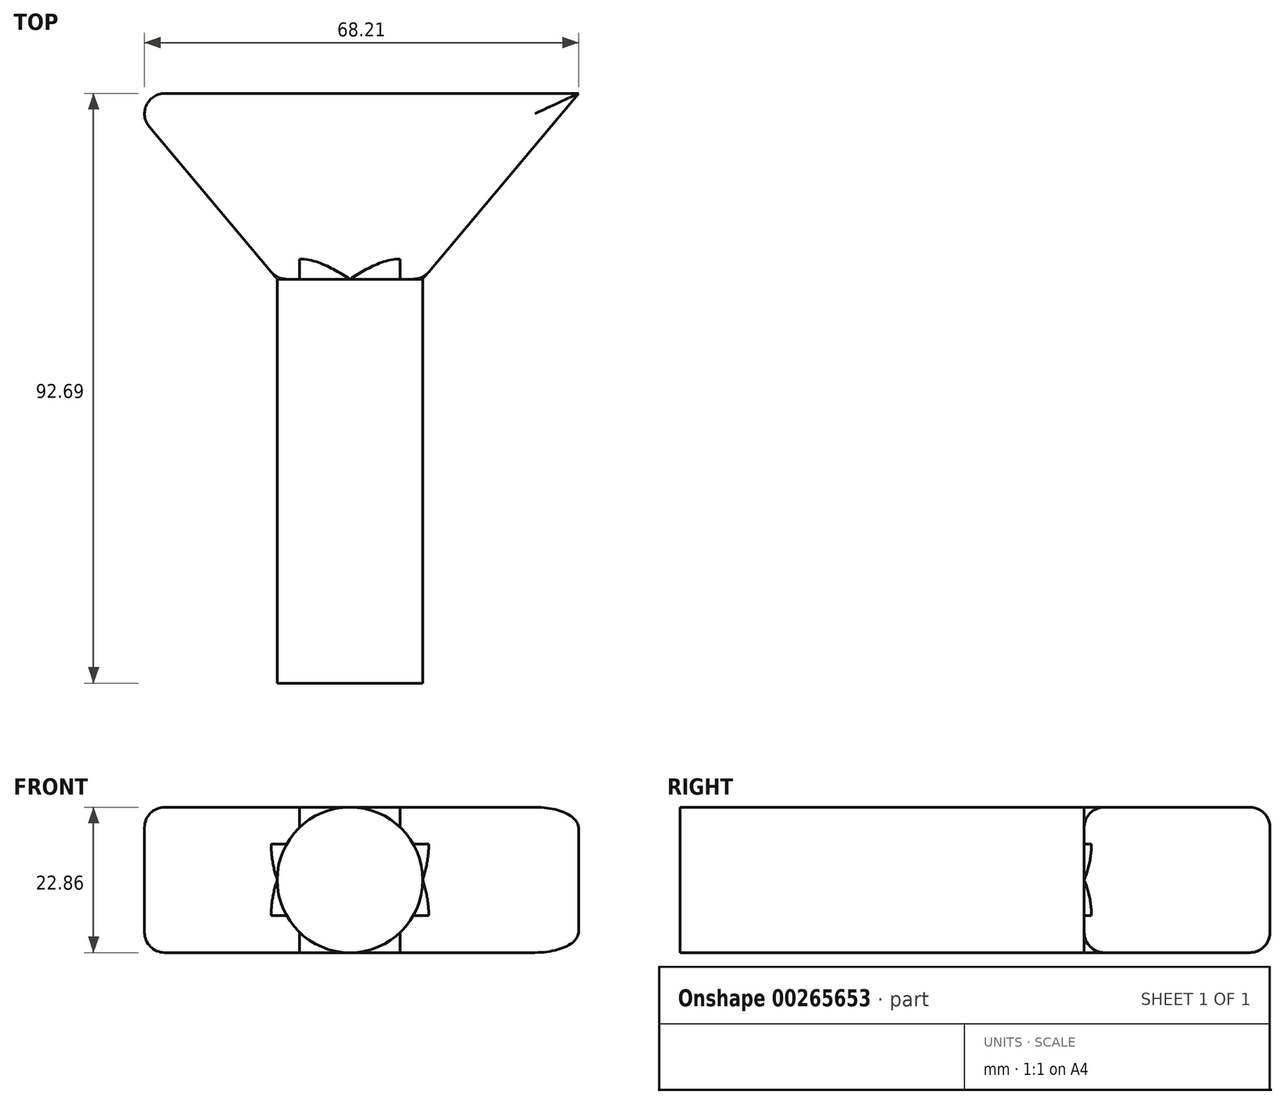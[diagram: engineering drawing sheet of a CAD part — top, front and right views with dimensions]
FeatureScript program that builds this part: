
annotation { "Feature Type Name" : "Feature", "Feature Type Description" : "" }
export const myFeature = defineFeature(function(context is Context, id is Id, definition is map)
    precondition{}
    {
        {
            var Q0;
            Q0=qCreatedBy(makeId("Top.planeOp"),FACE);
            var sketch = newSketch(context, id + "F0", { "sketchPlane" : qUnion([Q0])});
            skLineSegment(sketch, "E0", {"start": v(11.43, 0) * mm, "end": v(35.92, 29.19) * mm});
            skLineSegment(sketch, "E1", {"start": v(-11.43, 0) * mm, "end": v(-35.92, 29.19) * mm});
            skLineSegment(sketch, "E2", {"start": v(-35.92, 29.19) * mm, "end": v(35.92, 29.19) * mm});
            skLineSegment(sketch, "E3", {"start": v(-11.43, 0) * mm, "end": v(11.43, 0) * mm});
            skSolve(sketch);
        }
        {
            var Q0;
            Q0 = qSketchRegion(id + "F0", true);
            extrude(context, id + "F1", {"entities" : qUnion([Q0]), "depth" : 22.86 * mm});
        }
        {
            var Q0;
            Q0=makeQuery(id+"F1.opExtrude","SWEPT_FACE",FACE,{"disambiguationData":[OSD([sQuery(id+"F0.wireOp",EDGE,"E3")])]});
            var sketch = newSketch(context, id + "F2", { "sketchPlane" : qUnion([Q0])});
            skCircle(sketch, "E4", {"center": v(0, 11.43) * mm, "radius": 11.43 * mm});
            skPoint(sketch, "E4.centerSnap0", {"position": v(-11.43, 11.43) * mm});
            skSolve(sketch);
        }
        {
            var Q0;
            {var subQ0=sQuery(id+"F2.wireOp",EDGE,"E4");var subQ1=sQuery(id+"F0.wireOp",EDGE,"E3");var subQ2=makeQuery(id+"F2.imprint","INTERSECT",VERTEX,{"derivedFrom":[makeQuery(id+"F1.opExtrude","CAP_EDGE",EDGE,{"disambiguationData":[OSD([subQ1])],"isStart":false}),subQ0]});Q0=makeQuery(id+"F2.imprint","IMPRINT",FACE,{"disambiguationData":[TD([[makeQuery(id+"F2.imprint","IMPRINT",EDGE,{"disambiguationData":[TD([[subQ2,1.0]])],"derivedFrom":subQ0}),1.0]])]});}
            extrude(context, id + "F3", {"entities" : qUnion([Q0]), "operationType" : NewBodyOperationType.ADD, "depth" : 63.5 * mm});
        }
        {
            var Q0;
            Q0=makeQuery(id+"F1.opExtrude","CAP_EDGE",EDGE,{"disambiguationData":[OSD([sQuery(id+"F0.wireOp",EDGE,"E0")])],"isStart":false});
            var Q1;
            Q1=makeQuery(id+"F1.opExtrude","CAP_EDGE",EDGE,{"disambiguationData":[OSD([sQuery(id+"F0.wireOp",EDGE,"E1")])],"isStart":false});
            var Q2;
            Q2=makeQuery(id+"F1.opExtrude","CAP_FACE",FACE,{"disambiguationData":[OSD([sQuery(id+"F0.wireOp",EDGE,"E0"),sQuery(id+"F0.wireOp",EDGE,"E1"),sQuery(id+"F0.wireOp",EDGE,"E2"),sQuery(id+"F0.wireOp",EDGE,"E3")])],"isStart":false});
            var Q3;
            Q3=makeQuery(id+"F1.opExtrude","CAP_EDGE",EDGE,{"disambiguationData":[OSD([sQuery(id+"F0.wireOp",EDGE,"E1")])],"isStart":true});
            var Q4;
            Q4=makeQuery(id+"F1.opExtrude","SWEPT_EDGE",EDGE,{"disambiguationData":[OSD([sQuery(id+"F0.wireOp",EDGE,"E1"),sQuery(id+"F0.wireOp",EDGE,"E2")])]});
            var Q5;
            {var subQ0=sQuery(id+"F0.wireOp",EDGE,"E3");var subQ1=sQuery(id+"F0.wireOp",EDGE,"E1");Q5=makeQuery(id+"F3.boolean.opBoolean","SPLIT",EDGE,{"disambiguationData":[TD([makeQuery(id+"F1.opExtrude","CAP_FACE",FACE,{"disambiguationData":[OSD([sQuery(id+"F0.wireOp",EDGE,"E0"),subQ1,sQuery(id+"F0.wireOp",EDGE,"E2"),subQ0])],"isStart":false})])],"derivedFrom":makeQuery(id+"F1.opExtrude","SWEPT_EDGE",EDGE,{"disambiguationData":[OSD([subQ1,subQ0])]})});}
            var Q6;
            {var subQ0=sQuery(id+"F0.wireOp",EDGE,"E0");var subQ1=sQuery(id+"F0.wireOp",EDGE,"E3");Q6=makeQuery(id+"F3.boolean.opBoolean","SPLIT",EDGE,{"disambiguationData":[TD([makeQuery(id+"F1.opExtrude","CAP_FACE",FACE,{"disambiguationData":[OSD([subQ0,sQuery(id+"F0.wireOp",EDGE,"E1"),sQuery(id+"F0.wireOp",EDGE,"E2"),subQ1])],"isStart":false})])],"derivedFrom":makeQuery(id+"F1.opExtrude","SWEPT_EDGE",EDGE,{"disambiguationData":[OSD([subQ0,subQ1])]})});}
            var Q7;
            {var subQ0=sQuery(id+"F0.wireOp",EDGE,"E0");var subQ1=sQuery(id+"F0.wireOp",EDGE,"E3");Q7=makeQuery(id+"F3.boolean.opBoolean","SPLIT",EDGE,{"disambiguationData":[TD([makeQuery(id+"F1.opExtrude","CAP_FACE",FACE,{"disambiguationData":[OSD([subQ0,sQuery(id+"F0.wireOp",EDGE,"E1"),sQuery(id+"F0.wireOp",EDGE,"E2"),subQ1])],"isStart":true})])],"derivedFrom":makeQuery(id+"F1.opExtrude","SWEPT_EDGE",EDGE,{"disambiguationData":[OSD([subQ0,subQ1])]})});}
            var Q8;
            {var subQ0=sQuery(id+"F0.wireOp",EDGE,"E0");var subQ1=sQuery(id+"F0.wireOp",EDGE,"E3");Q8=makeQuery(id+"F3.boolean.opBoolean","SPLIT",EDGE,{"disambiguationData":[TD([makeQuery(id+"F1.opExtrude","SWEPT_FACE",FACE,{"disambiguationData":[OSD([subQ0])]})])],"derivedFrom":makeQuery(id+"F1.opExtrude","CAP_EDGE",EDGE,{"disambiguationData":[OSD([subQ1])],"isStart":true})});}
            var Q9;
            {var subQ0=sQuery(id+"F0.wireOp",EDGE,"E3");var subQ1=sQuery(id+"F0.wireOp",EDGE,"E1");Q9=makeQuery(id+"F3.boolean.opBoolean","SPLIT",EDGE,{"disambiguationData":[TD([makeQuery(id+"F1.opExtrude","SWEPT_FACE",FACE,{"disambiguationData":[OSD([subQ1])]})])],"derivedFrom":makeQuery(id+"F1.opExtrude","CAP_EDGE",EDGE,{"disambiguationData":[OSD([subQ0])],"isStart":true})});}
            var Q10;
            {var subQ0=sQuery(id+"F0.wireOp",EDGE,"E3");var subQ1=sQuery(id+"F0.wireOp",EDGE,"E1");Q10=makeQuery(id+"F3.boolean.opBoolean","SPLIT",EDGE,{"disambiguationData":[TD([makeQuery(id+"F1.opExtrude","CAP_FACE",FACE,{"disambiguationData":[OSD([sQuery(id+"F0.wireOp",EDGE,"E0"),subQ1,sQuery(id+"F0.wireOp",EDGE,"E2"),subQ0])],"isStart":true})])],"derivedFrom":makeQuery(id+"F1.opExtrude","SWEPT_EDGE",EDGE,{"disambiguationData":[OSD([subQ1,subQ0])]})});}
            var Q11;
            {var subQ0=sQuery(id+"F0.wireOp",EDGE,"E3");var subQ1=sQuery(id+"F0.wireOp",EDGE,"E1");Q11=makeQuery(id+"F3.boolean.opBoolean","SPLIT",EDGE,{"disambiguationData":[TD([makeQuery(id+"F1.opExtrude","SWEPT_FACE",FACE,{"disambiguationData":[OSD([subQ1])]})])],"derivedFrom":makeQuery(id+"F1.opExtrude","CAP_EDGE",EDGE,{"disambiguationData":[OSD([subQ0])],"isStart":false})});}
            var Q12;
            {var subQ0=sQuery(id+"F0.wireOp",EDGE,"E0");var subQ1=sQuery(id+"F0.wireOp",EDGE,"E3");Q12=makeQuery(id+"F3.boolean.opBoolean","SPLIT",EDGE,{"disambiguationData":[TD([makeQuery(id+"F1.opExtrude","SWEPT_FACE",FACE,{"disambiguationData":[OSD([subQ0])]})])],"derivedFrom":makeQuery(id+"F1.opExtrude","CAP_EDGE",EDGE,{"disambiguationData":[OSD([subQ1])],"isStart":false})});}
            var Q13;
            Q13=makeQuery(id+"F1.opExtrude","CAP_EDGE",EDGE,{"disambiguationData":[OSD([sQuery(id+"F0.wireOp",EDGE,"E0")])],"isStart":true});
            var Q14;
            Q14=makeQuery(id+"F1.opExtrude","CAP_EDGE",EDGE,{"disambiguationData":[OSD([sQuery(id+"F0.wireOp",EDGE,"E2")])],"isStart":true});
            fillet(context, id + "F4", {"entities" : qUnion([Q0, Q1, Q2, Q3, Q4, Q5, Q6, Q7, Q8, Q9, Q10, Q11, Q12, Q13, Q14]), "radius" : 3.17 * mm, "tangentPropagation" : true, "allowEdgeOverflow" : false});
        }
    });
